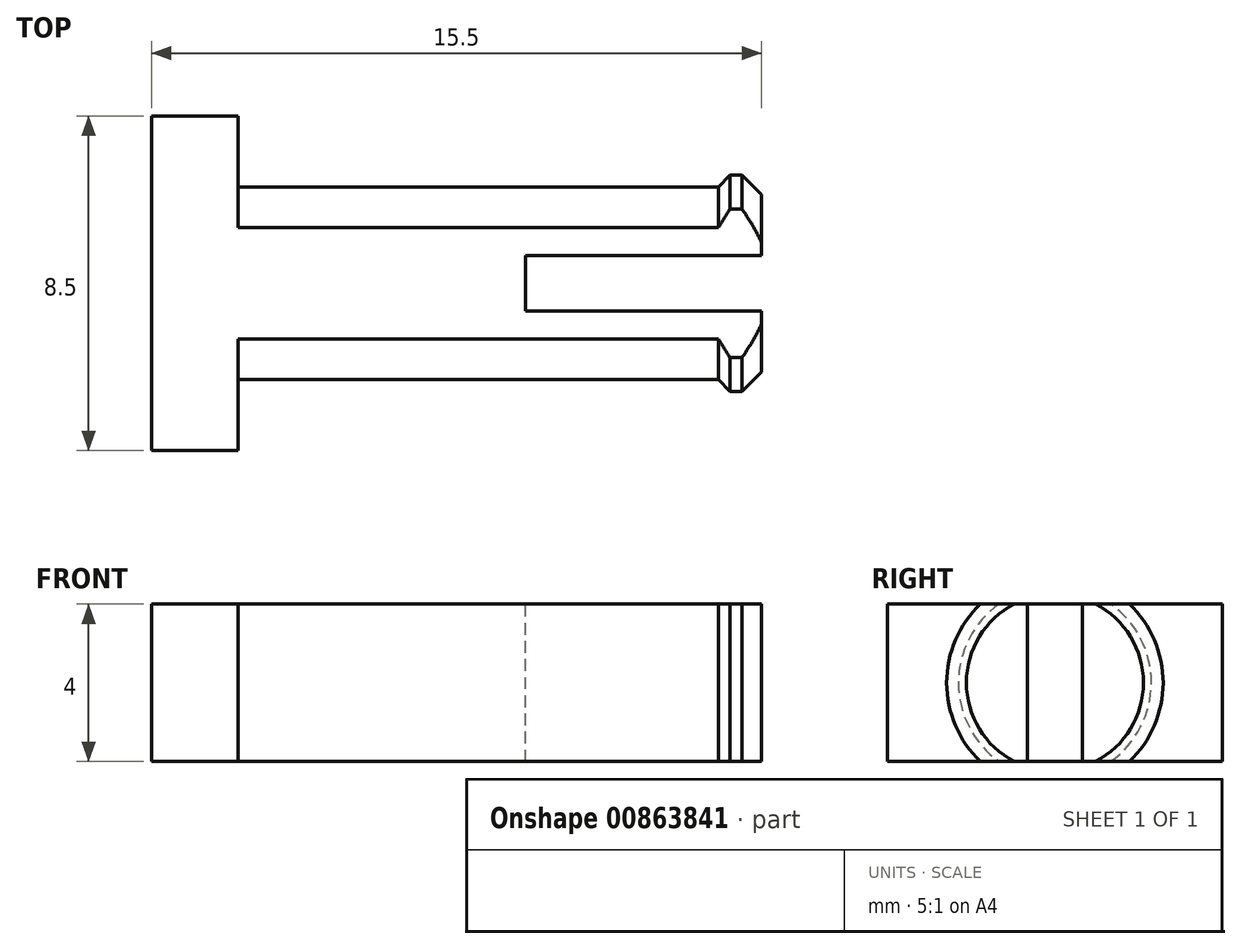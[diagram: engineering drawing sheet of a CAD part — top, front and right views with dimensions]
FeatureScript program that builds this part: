
annotation { "Feature Type Name" : "Feature", "Feature Type Description" : "" }
export const myFeature = defineFeature(function(context is Context, id is Id, definition is map)
    precondition{}
    {
        {
            assignVariable(context, id + "F0", {"name" : "pin_diameter", "anyValue" : 5});
        }
        {
            var Q0;
            Q0=qCreatedBy(makeId("Front.planeOp"),FACE);
            var sketch = newSketch(context, id + "F1", { "sketchPlane" : qUnion([Q0])});
            skLineSegment(sketch, "E0", {"start": v(0, 0) * mm, "end": v(17.77, 0) * mm, "construction": true});
            skLineSegment(sketch, "E1", {"start": v(0, 0) * mm, "end": v(0, 7.5) * mm});
            skLineSegment(sketch, "E2", {"start": v(0, 7.5) * mm, "end": v(2.2, 7.5) * mm});
            skLineSegment(sketch, "E3", {"start": v(2.2, 7.5) * mm, "end": v(2.2, 2.45) * mm});
            skLineSegment(sketch, "E4", {"start": v(2.2, 2.45) * mm, "end": v(14.2, 2.45) * mm});
            skLineSegment(sketch, "E5", {"start": v(14.2, 2.45) * mm, "end": v(14.2, 2.75) * mm});
            skLineSegment(sketch, "E6", {"start": v(14.2, 2.75) * mm, "end": v(15.5, 2.75) * mm});
            skLineSegment(sketch, "E7", {"start": v(15.5, 2.75) * mm, "end": v(15.5, 0) * mm});
            skLineSegment(sketch, "E8", {"start": v(15.5, 0) * mm, "end": v(0, 0) * mm});
            skSolve(sketch);
        }
        {
            var Q0;
            Q0=makeQuery(id+"F1.imprint","IMPRINT",FACE,{"disambiguationData":[TD([[makeQuery(id+"F1.imprint","IMPRINT",EDGE,{"derivedFrom":sQuery(id+"F1.wireOp",EDGE,"E1")}),-1.0]])]});
            var Q1;
            Q1=sQuery(id+"F1.wireOp",EDGE,"E0");
            revolve(context, id + "F2", {"surfaceOperationType" : NewSurfaceOperationType.NEW, "entities" : qUnion([Q0]), "axis" : qUnion([Q1]), "revolveType" : RevolveType.FULL});
        }
        {
            var Q0;
            Q0=qCreatedBy(makeId("Right.planeOp"),FACE);
            var sketch = newSketch(context, id + "F3", { "sketchPlane" : qUnion([Q0])});
            skLineSegment(sketch, "E9.bottom", {"start": v(-4.25, 2) * mm, "end": v(4.25, 2) * mm});
            skLineSegment(sketch, "E9.top", {"start": v(-4.25, -2) * mm, "end": v(4.25, -2) * mm});
            skLineSegment(sketch, "E9.left", {"start": v(-4.25, 2) * mm, "end": v(-4.25, -2) * mm});
            skLineSegment(sketch, "E9.right", {"start": v(4.25, 2) * mm, "end": v(4.25, -2) * mm});
            skLineSegment(sketch, "E10", {"start": v(0, 2) * mm, "end": v(0, 0) * mm, "construction": true});
            skLineSegment(sketch, "E11", {"start": v(0, 0) * mm, "end": v(4.25, 0) * mm, "construction": true});
            skLineSegment(sketch, "E12.0", {"start": v(-19.25, 17) * mm, "end": v(19.25, 17) * mm});
            skLineSegment(sketch, "E12.1", {"start": v(-19.25, 17) * mm, "end": v(-19.25, -17) * mm});
            skLineSegment(sketch, "E12.2", {"start": v(-19.25, -17) * mm, "end": v(19.25, -17) * mm});
            skLineSegment(sketch, "E12.3", {"start": v(19.25, 17) * mm, "end": v(19.25, -17) * mm});
            skSolve(sketch);
        }
        {
            var Q0;
            Q0 = qSketchRegion(id + "F3", true);
            extrude(context, id + "F4", {"entities" : qUnion([Q0]), "operationType" : NewBodyOperationType.REMOVE, "endBound" : BoundingType.THROUGH_ALL, "depth" : (getVariable(context, 'pin_diameter') * 2) * mm, "offsetDistance" : 25 * mm});
        }
        {
            var Q0;
            Q0=makeQuery(id+"F4.boolean.opBoolean","SPLIT",EDGE,{"disambiguationData":[OD(0.0)],"derivedFrom":makeQuery(id+"F2.opRevolve","SWEPT_EDGE",EDGE,{"disambiguationData":[OSD([sQuery(id+"F1.wireOp",EDGE,"E5"),sQuery(id+"F1.wireOp",EDGE,"E6")])]})});
            var Q1;
            Q1=makeQuery(id+"F4.boolean.opBoolean","SPLIT",EDGE,{"disambiguationData":[OD(0.0)],"derivedFrom":makeQuery(id+"F2.opRevolve","SWEPT_EDGE",EDGE,{"disambiguationData":[OSD([sQuery(id+"F1.wireOp",EDGE,"E6"),sQuery(id+"F1.wireOp",EDGE,"E7")])]})});
            var Q2;
            Q2=makeQuery(id+"F4.boolean.opBoolean","SPLIT",EDGE,{"disambiguationData":[OD(1.0)],"derivedFrom":makeQuery(id+"F2.opRevolve","SWEPT_EDGE",EDGE,{"disambiguationData":[OSD([sQuery(id+"F1.wireOp",EDGE,"E5"),sQuery(id+"F1.wireOp",EDGE,"E6")])]})});
            var Q3;
            Q3=makeQuery(id+"F4.boolean.opBoolean","SPLIT",EDGE,{"disambiguationData":[OD(1.0)],"derivedFrom":makeQuery(id+"F2.opRevolve","SWEPT_EDGE",EDGE,{"disambiguationData":[OSD([sQuery(id+"F1.wireOp",EDGE,"E6"),sQuery(id+"F1.wireOp",EDGE,"E7")])]})});
            chamfer(context, id + "F5", {"entities" : qUnion([Q0, Q1, Q2, Q3]), "width" : 0.5 * mm, "tangentPropagation" : true});
        }
        {
            var Q0;
            Q0=makeQuery(id+"F4.boolean.opBoolean","COPY",FACE,{"derivedFrom":makeQuery(id+"F4.opExtrude","SWEPT_FACE",FACE,{"disambiguationData":[OSD([sQuery(id+"F3.wireOp",EDGE,"E9.bottom")])]})});
            var sketch = newSketch(context, id + "F6", { "sketchPlane" : qUnion([Q0])});
            skLineSegment(sketch, "E13.bottom", {"start": v(15.5, 0.7) * mm, "end": v(9.5, 0.7) * mm});
            skLineSegment(sketch, "E13.top", {"start": v(15.5, -0.7) * mm, "end": v(9.5, -0.7) * mm});
            skLineSegment(sketch, "E13.left", {"start": v(15.5, 0.7) * mm, "end": v(15.5, -0.7) * mm});
            skLineSegment(sketch, "E13.right", {"start": v(9.5, 0.7) * mm, "end": v(9.5, -0.7) * mm});
            skLineSegment(sketch, "E14", {"start": v(0, 0) * mm, "end": v(15.5, 0) * mm, "construction": true});
            skSolve(sketch);
        }
        {
            var Q0;
            Q0 = qSketchRegion(id + "F6", true);
            extrude(context, id + "F7", {"entities" : qUnion([Q0]), "operationType" : NewBodyOperationType.REMOVE, "endBound" : BoundingType.THROUGH_ALL, "oppositeDirection" : true, "depth" : 25 * mm, "offsetDistance" : 25 * mm});
        }
    });
